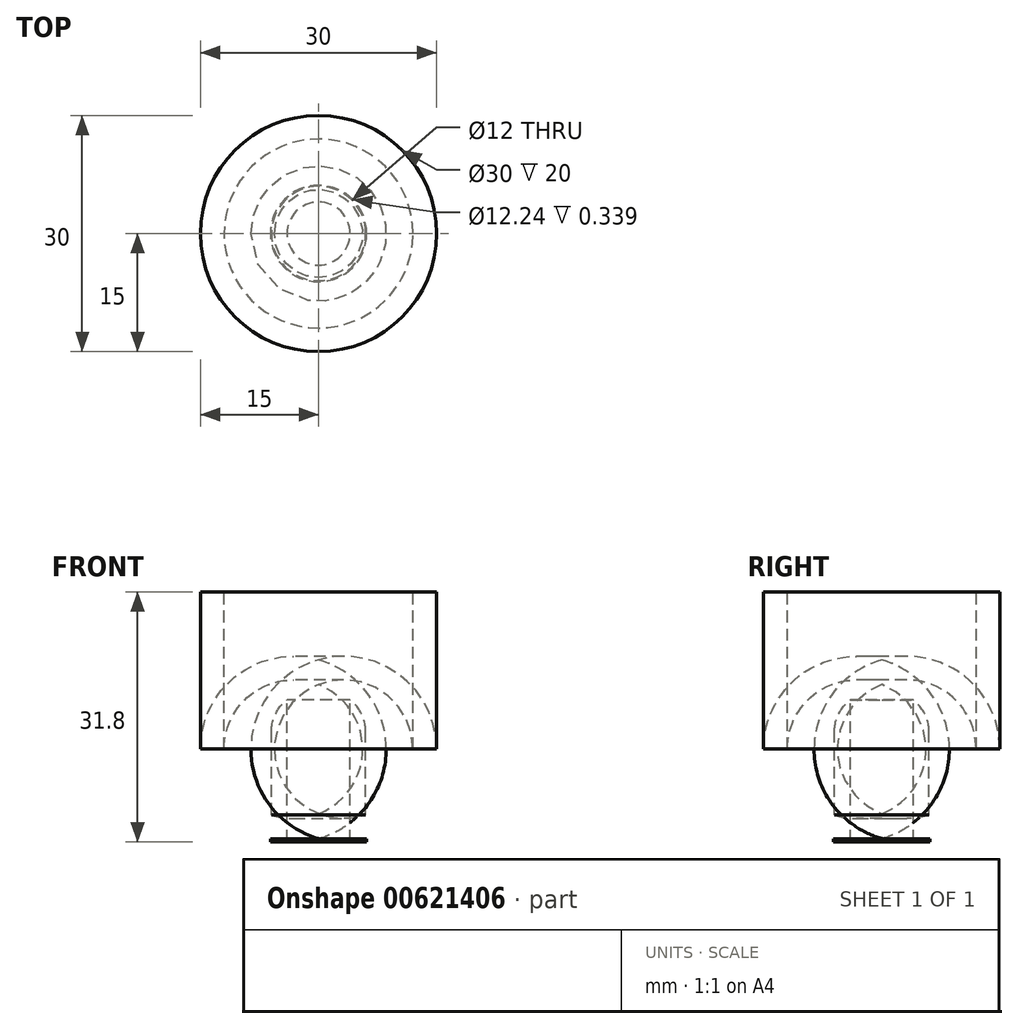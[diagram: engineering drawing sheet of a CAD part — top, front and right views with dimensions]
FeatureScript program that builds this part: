
annotation { "Feature Type Name" : "Feature", "Feature Type Description" : "" }
export const myFeature = defineFeature(function(context is Context, id is Id, definition is map)
    precondition{}
    {
        {
            var Q0;
            Q0=qCreatedBy(makeId("Front.planeOp"),FACE);
            var sketch = newSketch(context, id + "F0", { "sketchPlane" : qUnion([Q0])});
            skLineSegment(sketch, "E0", {"start": v(13.5, 0) * mm, "end": v(15, 0) * mm});
            skLineSegment(sketch, "E1", {"start": v(15, 0) * mm, "end": v(15, -20) * mm});
            skArc(sketch, "E2", {"start": v(15, -20) * mm, "mid": v(12.52, -27.24) * mm, "end": v(6.12, -31.43) * mm});
            skLineSegment(sketch, "E3", {"start": v(4, -28.77) * mm, "end": v(4, -31.77) * mm});
            skArc(sketch, "E4", {"start": v(4, -28.77) * mm, "mid": v(9.7, -25.94) * mm, "end": v(12, -20) * mm});
            skLineSegment(sketch, "E5", {"start": v(12, -20) * mm, "end": v(12, -1.5) * mm});
            skPoint(sketch, "E6.orphan", {"position": v(12, 0) * mm});
            skPoint(sketch, "E7.end.orphan", {"position": v(13.18, 0) * mm});
            skPoint(sketch, "E8.start.orphan", {"position": v(0, -3) * mm});
            skLineSegment(sketch, "E9", {"start": v(4, -61.63) * mm, "end": v(6, -61.63) * mm});
            skPoint(sketch, "E10.end.orphan", {"position": v(0, -31.77) * mm});
            skLineSegment(sketch, "E11", {"start": v(0, 12.27) * mm, "end": v(0, -66.41) * mm});
            skLineSegment(sketch, "E12", {"start": v(4, -28.77) * mm, "end": v(4, -13.77) * mm});
            skLineSegment(sketch, "E13", {"start": v(4, -13.77) * mm, "end": v(6, -13.77) * mm});
            skLineSegment(sketch, "E14", {"start": v(6, -13.77) * mm, "end": v(6, -28.35) * mm});
            skPoint(sketch, "E15.end.orphan", {"position": v(6, -31.77) * mm});
            skPoint(sketch, "E16.start.orphan", {"position": v(6, -31.63) * mm});
            skLineSegment(sketch, "E17", {"start": v(6.12, -31.43) * mm, "end": v(6.12, -31.77) * mm});
            skLineSegment(sketch, "E18", {"start": v(4, -31.77) * mm, "end": v(6.12, -31.77) * mm});
            skPoint(sketch, "E19.orphan", {"position": v(6.12, -32.04) * mm});
            skLineSegment(sketch, "E20", {"start": v(13.5, 0) * mm, "end": v(12, 0) * mm});
            skLineSegment(sketch, "E21", {"start": v(12, -1.5) * mm, "end": v(12, 0) * mm});
            skSolve(sketch);
        }
        {
            var Q0;
            Q0=makeQuery(id+"F0.imprint","IMPRINT",FACE,{"disambiguationData":[TD([[makeQuery(id+"F0.imprint","IMPRINT",EDGE,{"derivedFrom":sQuery(id+"F0.wireOp",EDGE,"E1")}),-1.0]])]});
            var Q1;
            {var subQ0=sQuery(id+"F0.wireOp",EDGE,"E12");Q1=makeQuery(id+"F0.imprint","IMPRINT",FACE,{"disambiguationData":[TD([[makeQuery(id+"F0.imprint","IMPRINT",EDGE,{"derivedFrom":subQ0}),-1.0]])]});}
            var Q2;
            Q2=sQuery(id+"F0.wireOp",EDGE,"E11");
            revolve(context, id + "F1", {"entities" : qUnion([Q0, Q1]), "axis" : qUnion([Q2]), "revolveType" : RevolveType.FULL});
        }
        {
            var Q0;
            Q0=makeQuery(id+"F1.opRevolve","SWEPT_EDGE",EDGE,{"disambiguationData":[OSD([sQuery(id+"F0.wireOp",EDGE,"E13"),sQuery(id+"F0.wireOp",EDGE,"E14")])]});
            fillet(context, id + "F2", {"entities" : qUnion([Q0]), "radius" : 5 * mm, "tangentPropagation" : true, "allowEdgeOverflow" : false});
        }
    });
